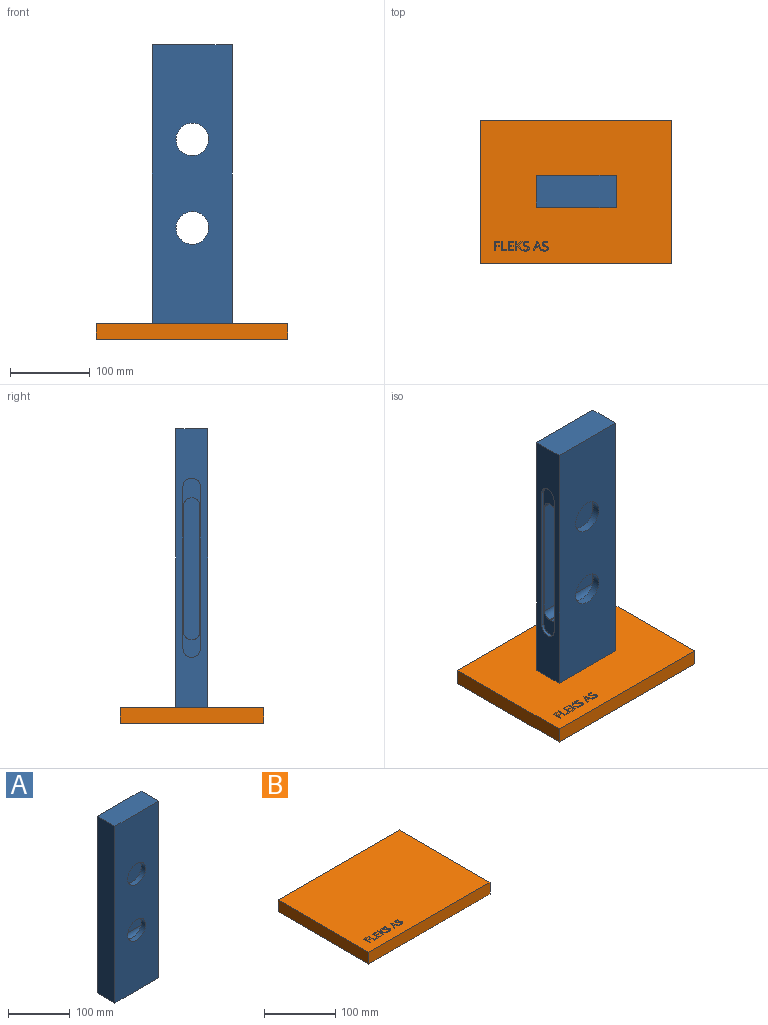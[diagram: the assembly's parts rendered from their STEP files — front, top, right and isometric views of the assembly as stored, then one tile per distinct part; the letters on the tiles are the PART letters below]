
ASSEMBLY  parts=2 mates=1
PART A: 24 faces, bbox 100x40x350 mm
  f0: plane 225x22mm, normal (1,0,0), area 1355.7mm2, adj f11,f12,f13,f14,f15,f16,f17,f18
  f1: cylinder r=20.5mm len=41mm, axis (0,1,0), area 1288.1mm2, adj f10,f21
  f2: cylinder r=20.5mm len=41mm, axis (0,1,0), area 1288.1mm2, adj f10,f21
  f3: plane 100x40mm, normal (0,0,-1), area 4000mm2, adj f4,f8,f9,f10
  f4: plane 350x40mm, normal (1,0,0), area 9153.9mm2, adj f3,f5,f9,f10,f11,f12,f13,f14
  f5: plane 100x40mm, normal (0,0,1), area 4000mm2, adj f4,f8,f9,f10
  f6: cylinder r=20.5mm len=41mm, axis (0,1,0), area 1288.1mm2, adj f9,f17
  f7: cylinder r=20.5mm len=41mm, axis (0,1,0), area 1288.1mm2, adj f9,f17
  f8: plane 350x40mm, normal (-1,0,0), area 14000mm2, adj f3,f5,f9,f10
  f9: plane 350x100mm, normal (0,-1,0), area 32359.5mm2, adj f3,f4,f5,f6,f7,f8
  f10: plane 350x100mm, normal (0,1,0), area 32359.5mm2, adj f1,f2,f3,f4,f5,f8
  f11: cylinder r=11mm len=22mm, axis (1,0,0), area 138.2mm2, adj f0,f4,f12,f14
  f12: plane 203x4mm, normal (0,1,0), area 812mm2, adj f0,f4,f11,f13
  f13: cylinder r=11mm len=22mm, axis (1,0,0), area 138.2mm2, adj f0,f4,f12,f14
  f14: plane 203x4mm, normal (0,-1,0), area 812mm2, adj f0,f4,f11,f13
  f15: plane 85x2mm, normal (0,0,-1), area 170mm2, adj f0,f16,f22,f23
  f16: cylinder r=9mm len=85mm, axis (1,0,0), area 1201.7mm2, adj f0,f15,f17,f23
  f17: plane 160x85mm, normal (0,1,0), area 10959.5mm2, adj f0,f6,f7,f16,f18,f23
  f18: cylinder r=9mm len=85mm, axis (1,0,0), area 1201.7mm2, adj f0,f17,f19,f23
  f19: plane 85x2mm, normal (0,0,1), area 170mm2, adj f0,f18,f20,f23
  f20: cylinder r=9mm len=85mm, axis (1,0,0), area 1201.7mm2, adj f0,f19,f21,f23
  f21: plane 160x85mm, normal (0,-1,0), area 10959.5mm2, adj f0,f1,f2,f20,f22,f23
  f22: cylinder r=9mm len=85mm, axis (1,0,0), area 1201.7mm2, adj f0,f15,f21,f23
  f23: plane 178x20mm, normal (1,0,0), area 3490.5mm2, adj f15,f16,f17,f18,f19,f20,f21,f22
PART B: 117 faces, bbox 240x180x20 mm
  f0: plane 240x180mm, normal (0,0,1), area 42963.4mm2, adj f1,f2,f3,f4,f10,f11,f12,f13
  f1: plane 240x20mm, normal (0,1,0), area 4800mm2, adj f0,f2,f4,f5
  f2: plane 180x20mm, normal (-1,0,0), area 3600mm2, adj f0,f1,f3,f5
  f3: plane 240x20mm, normal (0,-1,0), area 4800mm2, adj f0,f2,f4,f5
  f4: plane 180x20mm, normal (1,0,0), area 3600mm2, adj f0,f1,f3,f5
  f5: plane 240x180mm, normal (0,0,-1), area 43200mm2, adj f1,f2,f3,f4
  f6: plane 3.69x2mm, normal (0.94,0.35,0), area 7.9mm2, adj f7,f18,f19,f116
  f7: plane 3.85x2mm, normal (0,-1,0), area 7.7mm2, adj f6,f8,f19,f116
  f8: plane 3.69x2mm, normal (-0.94,0.35,0), area 7.9mm2, adj f7,f9,f19,f116
  f9: extruded ~2x1.72mm, area 3.6mm2, adj f8,f18,f19,f116
  f10: plane 3.78x2mm, normal (0.93,0.36,0), area 8.1mm2, adj f0,f11,f17,f19
  f11: plane 2x1.43mm, normal (0,1,0), area 2.9mm2, adj f0,f10,f12,f19
  f12: plane 11.95x4.68mm, normal (-0.93,-0.36,0), area 25.7mm2, adj f0,f11,f13,f19
  f13: plane 2x1.16mm, normal (0,-1,0), area 2.3mm2, adj f0,f12,f14,f19
  f14: plane 11.95x4.7mm, normal (0.93,-0.37,0), area 25.7mm2, adj f0,f13,f15,f19
  f15: plane 2x1.4mm, normal (0,1,0), area 2.8mm2, adj f0,f14,f16,f19
  f16: plane 3.78x2mm, normal (-0.93,0.36,0), area 8.1mm2, adj f0,f15,f17,f19
  f17: plane 4.77x2mm, normal (0,1,0), area 9.5mm2, adj f0,f10,f16,f19
  f18: extruded ~2x1.72mm, area 3.6mm2, adj f6,f9,f19,f116
  f19: plane 11.95x10.55mm, normal (0,0,1), area 36.4mm2, adj f6,f7,f8,f9,f10,f11,f12,f13
  f20: extruded ~2.45x2mm, area 5.6mm2, adj f0,f21,f44,f45
  f21: extruded ~2x1.98mm, area 4.3mm2, adj f0,f20,f22,f45
  f22: extruded ~2.58x2mm, area 5.9mm2, adj f0,f21,f23,f45
  f23: extruded ~2x1.66mm, area 3.6mm2, adj f0,f22,f24,f45
  f24: extruded ~2x0.77mm, area 2.1mm2, adj f0,f23,f25,f45
  f25: extruded ~2x1.01mm, area 2.1mm2, adj f0,f24,f26,f45
  f26: extruded ~2x1.31mm, area 3mm2, adj f0,f25,f27,f45
  f27: extruded ~2x1.72mm, area 3.6mm2, adj f0,f26,f28,f45
  f28: extruded ~2.86x2mm, area 5.9mm2, adj f0,f27,f29,f45
  f29: plane 2x1.2mm, normal (-0.94,0.34,0), area 2.6mm2, adj f0,f28,f30,f45
  f30: extruded ~3.26x2mm, area 6.7mm2, adj f0,f29,f31,f45
  f31: extruded ~2.74x2mm, area 5.8mm2, adj f0,f30,f32,f45
  f32: extruded ~2.19x2mm, area 5mm2, adj f0,f31,f33,f45
  f33: extruded ~2.12x2mm, area 4.6mm2, adj f0,f32,f34,f45
  f34: extruded ~2.37x2mm, area 5.6mm2, adj f0,f33,f35,f45
  f35: extruded ~2x1.77mm, area 3.9mm2, adj f0,f34,f36,f45
  f36: extruded ~2x0.83mm, area 2.2mm2, adj f0,f35,f37,f45
  f37: extruded ~2x1.01mm, area 2.1mm2, adj f0,f36,f38,f45
  f38: extruded ~2x1.46mm, area 3.4mm2, adj f0,f37,f39,f45
  f39: extruded ~2.08x2mm, area 4.4mm2, adj f0,f38,f40,f45
  f40: extruded ~2x1.71mm, area 3.4mm2, adj f0,f39,f41,f45
  f41: extruded ~2x1.6mm, area 3.3mm2, adj f0,f40,f42,f45
  f42: plane 2x1.33mm, normal (1,0,0), area 2.7mm2, adj f0,f41,f43,f45
  f43: extruded ~3.26x2mm, area 6.7mm2, adj f0,f42,f44,f45
  f44: extruded ~3.09x2mm, area 6.5mm2, adj f0,f20,f43,f45
  f45: plane 12.23x7.49mm, normal (0,0,1), area 32.8mm2, adj f20,f21,f22,f23,f24,f25,f26,f27
  f46: extruded ~2.45x2mm, area 5.6mm2, adj f0,f47,f70,f71
  f47: extruded ~2x1.98mm, area 4.3mm2, adj f0,f46,f48,f71
  f48: extruded ~2.58x2mm, area 5.9mm2, adj f0,f47,f49,f71
  f49: extruded ~2x1.66mm, area 3.6mm2, adj f0,f48,f50,f71
  f50: extruded ~2x0.77mm, area 2.1mm2, adj f0,f49,f51,f71
  f51: extruded ~2x1.01mm, area 2.1mm2, adj f0,f50,f52,f71
  f52: extruded ~2x1.31mm, area 3mm2, adj f0,f51,f53,f71
  f53: extruded ~2x1.72mm, area 3.6mm2, adj f0,f52,f54,f71
  f54: extruded ~2.86x2mm, area 5.9mm2, adj f0,f53,f55,f71
  f55: plane 2x1.2mm, normal (-0.94,0.34,0), area 2.6mm2, adj f0,f54,f56,f71
  f56: extruded ~3.26x2mm, area 6.7mm2, adj f0,f55,f57,f71
  f57: extruded ~2.74x2mm, area 5.8mm2, adj f0,f56,f58,f71
  f58: extruded ~2.19x2mm, area 5mm2, adj f0,f57,f59,f71
  f59: extruded ~2.12x2mm, area 4.6mm2, adj f0,f58,f60,f71
  f60: extruded ~2.37x2mm, area 5.6mm2, adj f0,f59,f61,f71
  f61: extruded ~2x1.77mm, area 3.9mm2, adj f0,f60,f62,f71
  f62: extruded ~2x0.83mm, area 2.2mm2, adj f0,f61,f63,f71
  f63: extruded ~2x1.01mm, area 2.1mm2, adj f0,f62,f64,f71
  f64: extruded ~2x1.46mm, area 3.4mm2, adj f0,f63,f65,f71
  f65: extruded ~2.08x2mm, area 4.4mm2, adj f0,f64,f66,f71
  f66: extruded ~2x1.71mm, area 3.4mm2, adj f0,f65,f67,f71
  f67: extruded ~2x1.6mm, area 3.3mm2, adj f0,f66,f68,f71
  f68: plane 2x1.33mm, normal (1,0,0), area 2.7mm2, adj f0,f67,f69,f71
  f69: extruded ~3.26x2mm, area 6.7mm2, adj f0,f68,f70,f71
  f70: extruded ~3.09x2mm, area 6.5mm2, adj f0,f46,f69,f71
  f71: plane 12.23x7.49mm, normal (0,0,1), area 32.8mm2, adj f46,f47,f48,f49,f50,f51,f52,f53
  f72: plane 2x1.63mm, normal (0,1,0), area 3.3mm2, adj f0,f73,f83,f84
  f73: plane 6.73x4.96mm, normal (-0.8,-0.59,0), area 16.7mm2, adj f0,f72,f74,f84
  f74: plane 5.17x4.78mm, normal (-0.73,0.68,0), area 14.1mm2, adj f0,f73,f75,f84
  f75: plane 2x1.64mm, normal (0,-1,0), area 3.3mm2, adj f0,f74,f76,f84
  f76: plane 5.9x5.4mm, normal (0.74,-0.67,0), area 16mm2, adj f0,f75,f77,f84
  f77: plane 5.9x2mm, normal (-1,0,0), area 11.8mm2, adj f0,f76,f78,f84
  f78: plane 2x1.38mm, normal (0,-1,0), area 2.8mm2, adj f0,f77,f79,f84
  f79: plane 11.9x2mm, normal (1,0,0), area 23.8mm2, adj f0,f78,f80,f84
  f80: plane 2x1.38mm, normal (0,1,0), area 2.8mm2, adj f0,f79,f81,f84
  f81: plane 4.66x2mm, normal (-1,0,0), area 9.3mm2, adj f0,f80,f82,f84
  f82: plane 2x1.25mm, normal (-0.66,0.75,0), area 3.3mm2, adj f0,f81,f83,f84
  f83: plane 5.77x4.34mm, normal (0.8,0.6,0), area 14.4mm2, adj f0,f72,f82,f84
  f84: plane 11.9x8.59mm, normal (0,0,1), area 37.3mm2, adj f72,f73,f74,f75,f76,f77,f78,f79
  f85: plane 6.63x2mm, normal (0,1,0), area 13.3mm2, adj f0,f86,f96,f97
  f86: plane 2x1.24mm, normal (-1,0,0), area 2.5mm2, adj f0,f85,f87,f97
  f87: plane 5.25x2mm, normal (0,-1,0), area 10.5mm2, adj f0,f86,f88,f97
  f88: plane 4.38x2mm, normal (-1,0,0), area 8.8mm2, adj f0,f87,f89,f97
  f89: plane 4.93x2mm, normal (0,1,0), area 9.9mm2, adj f0,f88,f90,f97
  f90: plane 2x1.22mm, normal (-1,0,0), area 2.4mm2, adj f0,f89,f91,f97
  f91: plane 4.93x2mm, normal (0,-1,0), area 9.9mm2, adj f0,f90,f92,f97
  f92: plane 3.83x2mm, normal (-1,0,0), area 7.7mm2, adj f0,f91,f93,f97
  f93: plane 5.25x2mm, normal (0,1,0), area 10.5mm2, adj f0,f92,f94,f97
  f94: plane 2x1.23mm, normal (-1,0,0), area 2.5mm2, adj f0,f93,f95,f97
  f95: plane 6.63x2mm, normal (0,-1,0), area 13.3mm2, adj f0,f94,f96,f97
  f96: plane 11.9x2mm, normal (1,0,0), area 23.8mm2, adj f0,f85,f95,f97
  f97: plane 11.9x6.63mm, normal (0,0,1), area 35.4mm2, adj f85,f86,f87,f88,f89,f90,f91,f92
  f98: plane 11.9x2mm, normal (1,0,0), area 23.8mm2, adj f0,f99,f103,f104
  f99: plane 6.63x2mm, normal (0,1,0), area 13.3mm2, adj f0,f98,f100,f104
  f100: plane 2x1.25mm, normal (-1,0,0), area 2.5mm2, adj f0,f99,f101,f104
  f101: plane 5.25x2mm, normal (0,-1,0), area 10.5mm2, adj f0,f100,f102,f104
  f102: plane 10.65x2mm, normal (-1,0,0), area 21.3mm2, adj f0,f101,f103,f104
  f103: plane 2x1.38mm, normal (0,-1,0), area 2.8mm2, adj f0,f98,f102,f104
  f104: plane 11.9x6.63mm, normal (0,0,1), area 23mm2, adj f98,f99,f100,f101,f102,f103
  f105: plane 2x1.38mm, normal (0,1,0), area 2.8mm2, adj f0,f106,f114,f115
  f106: plane 5.09x2mm, normal (-1,0,0), area 10.2mm2, adj f0,f105,f107,f115
  f107: plane 4.93x2mm, normal (0,1,0), area 9.9mm2, adj f0,f106,f108,f115
  f108: plane 2x1.23mm, normal (-1,0,0), area 2.5mm2, adj f0,f107,f109,f115
  f109: plane 4.93x2mm, normal (0,-1,0), area 9.9mm2, adj f0,f108,f110,f115
  f110: plane 4.35x2mm, normal (-1,0,0), area 8.7mm2, adj f0,f109,f111,f115
  f111: plane 5.25x2mm, normal (0,1,0), area 10.5mm2, adj f0,f110,f112,f115
  f112: plane 2x1.23mm, normal (-1,0,0), area 2.5mm2, adj f0,f111,f113,f115
  f113: plane 6.63x2mm, normal (0,-1,0), area 13.3mm2, adj f0,f112,f114,f115
  f114: plane 11.9x2mm, normal (1,0,0), area 23.8mm2, adj f0,f105,f113,f115
  f115: plane 11.9x6.63mm, normal (0,0,1), area 29mm2, adj f105,f106,f107,f108,f109,f110,f111,f112
  f116: plane 5.4x3.85mm, normal (0,0,1), area 9.9mm2, adj f6,f7,f8,f9,f18
PLACE A rot(axis=(0,0,1),180deg) t=(-47.45,-9.56,-0.09)mm
PLACE B t=(6.76,-17.93,-0.09)mm
MATE fastened A.f3 <-> B.f0  axis (0,0,-1) through (2.55,10.44,-0.09)mm
